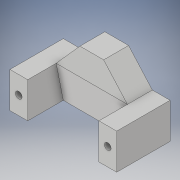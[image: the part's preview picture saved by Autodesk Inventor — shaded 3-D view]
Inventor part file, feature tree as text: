
AUTODESK INVENTOR PART (.ipt)
format: ipt  version: 2019 (Build 230136000, 136)  size: 174,080 bytes
history: native  units: in
note: dims shown in document units (in); Inventor stores cm internally (conversion verified against a paired STEP export)
features: sketch x6, extrude x4, hole x2, projected_geometry x1
ambient origin geometry x8: Origin, YZ Plane, XZ Plane, XY Plane, X Axis, Y Axis, Z Axis, Center Point
bodies: Solid1 (feature_tree)
feature tree (13):
  extrude  "Extrusion1"  Depth=1.5in
  extrude  "Extrusion2"  Depth=0.5in
  hole  "Hole1"  [1 undecoded]
  hole  "Hole2"  [1 undecoded]
  extrude  "Extrusion3"  Depth=0.5in
  extrude  "Extrusion4"  Depth=0.75in
  sketch  "Sketch1"  dims[d0=1.5in d1=1.5in]
  sketch  "Sketch2"  dims[d2=0.5in d3=0.5in]
  sketch  "Sketch3"  dims[d5=2.0in d6=0.5in]
  sketch  "Sketch4"  dims[d7=1.0in d8=0.0in d9=0.2in]
  sketch  "Sketch5"  dims[d10=2.0in d11=0.0in d12=0.5in]
  sketch  "Sketch6"  dims[d13=1.0in d14=0.25in d15=0.5in d16=0.5in d17=1.0in d18=0.5in d19=0.25in d20=0.1875in d21=0.75in d22=0.279in d23=0.25in d24=0.5635in d25=1.0in d26=0.8108in d27=1.5in d28=0.8in d29=3.0in d30=1.5in d31=0.35in d32=0.104in d33=0.276in d34=0.279in d35=0.25in d36=0.5635in d37=0.432in d38=0.8108in d39=0.5in d40=0.5in d41=0.75in d42=0.0in d43=2.0in d44=0.6667in d45=0.6667in d46=0.75in d47=0.0in]
  projected_geometry  "Projected Loop1"
note: 2 required parameter values undecoded (feature->parameter linkage not recoverable at this tier; creation-order binding heuristic only, values carry confidence <= 0.55)
